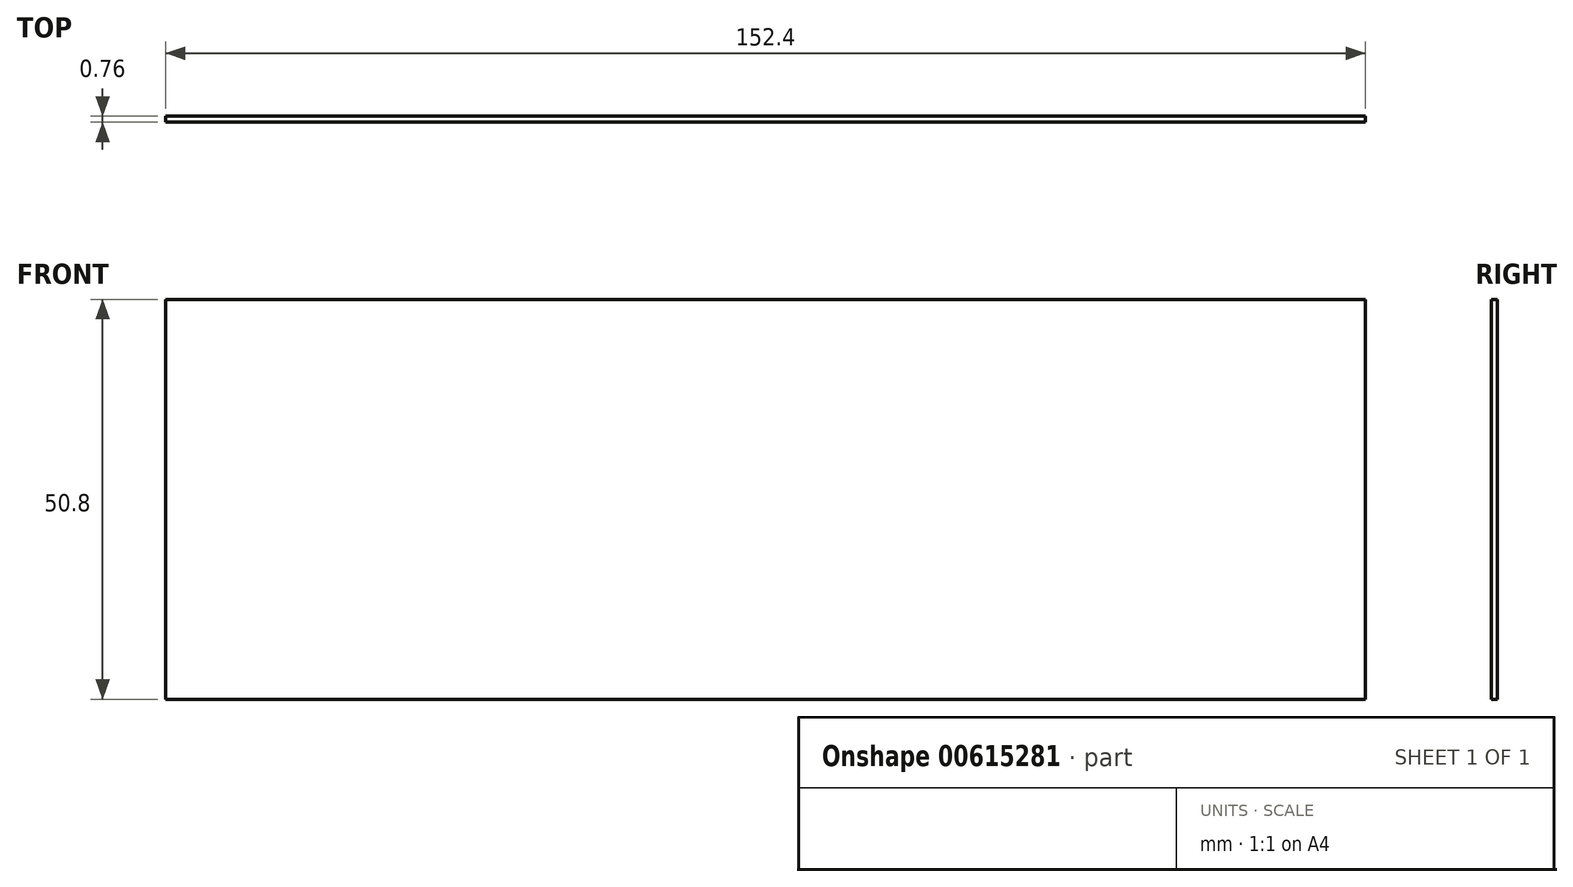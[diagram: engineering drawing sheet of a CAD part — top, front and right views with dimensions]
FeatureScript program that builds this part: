
annotation { "Feature Type Name" : "Feature", "Feature Type Description" : "" }
export const myFeature = defineFeature(function(context is Context, id is Id, definition is map)
    precondition{}
    {
        {
            assignVariable(context, id + "F0", {"name" : "Thickness", "anyValue" : 3 / 4});
        }
        {
            var Q0;
            Q0=qCreatedBy(makeId("Front.planeOp"),FACE);
            var sketch = newSketch(context, id + "F1", { "sketchPlane" : qUnion([Q0])});
            skLineSegment(sketch, "E0.bottom", {"start": v(-76.2, 25.4) * mm, "end": v(76.2, 25.4) * mm});
            skLineSegment(sketch, "E0.top", {"start": v(-76.2, -25.4) * mm, "end": v(76.2, -25.4) * mm});
            skLineSegment(sketch, "E0.left", {"start": v(-76.2, 25.4) * mm, "end": v(-76.2, -25.4) * mm});
            skLineSegment(sketch, "E0.right", {"start": v(76.2, 25.4) * mm, "end": v(76.2, -25.4) * mm});
            skLineSegment(sketch, "E1", {"start": v(-76.2, 25.4) * mm, "end": v(76.2, -25.4) * mm, "construction": true});
            skSolve(sketch);
        }
        {
            var Q0;
            Q0 = qSketchRegion(id + "F1", true);
            extrude(context, id + "F2", {"entities" : qUnion([Q0]), "endBound" : BoundingType.SYMMETRIC, "depth" : (getVariable(context, 'Thickness')) * mm, "offsetDistance" : 25.4 * mm});
        }
    });
